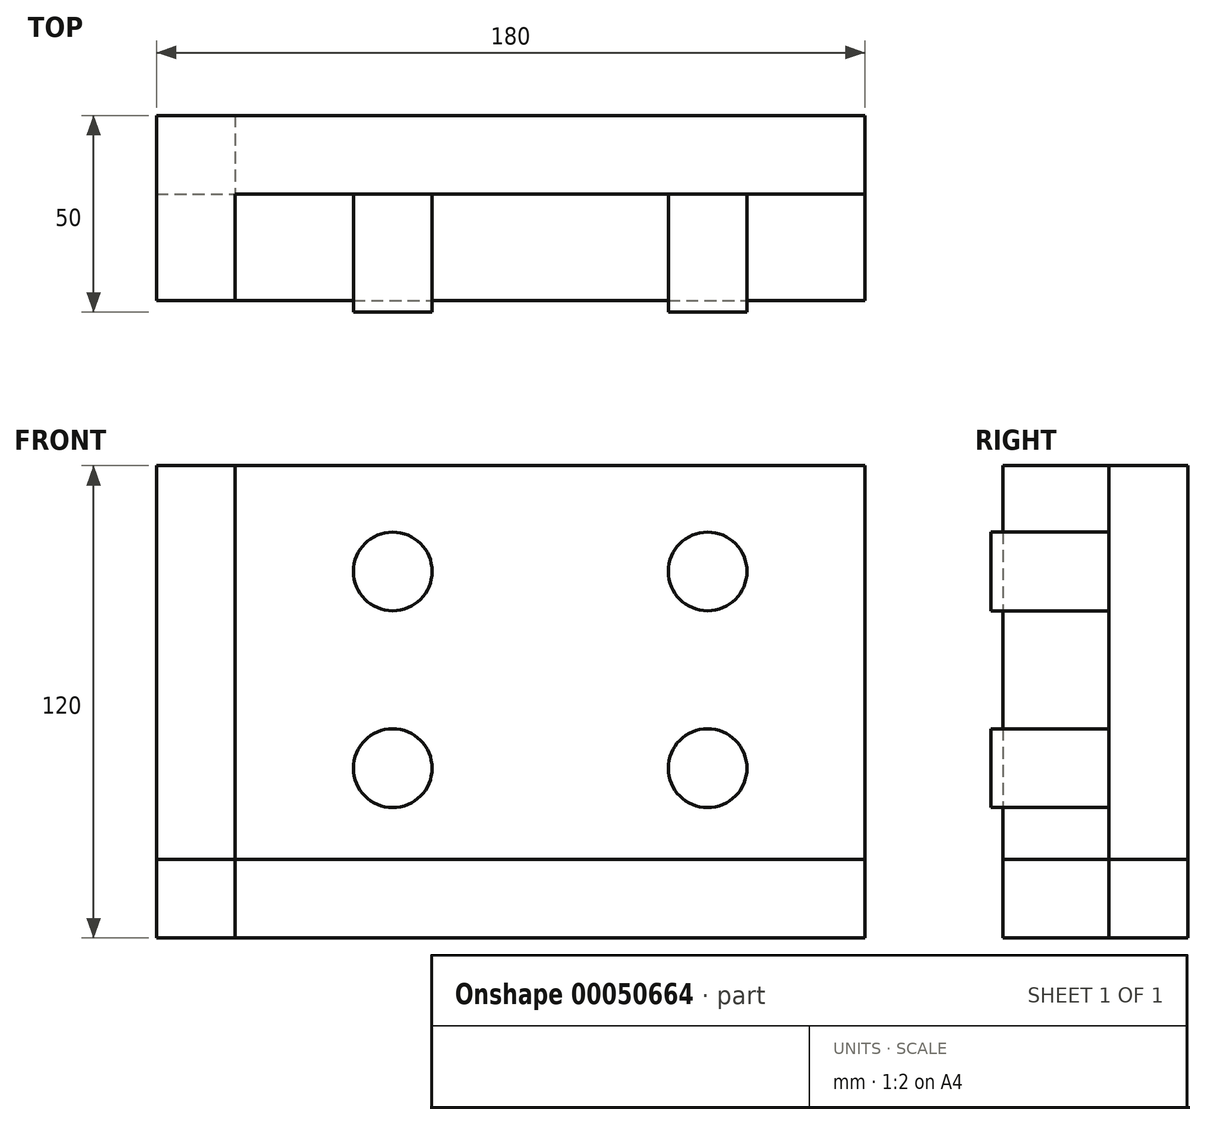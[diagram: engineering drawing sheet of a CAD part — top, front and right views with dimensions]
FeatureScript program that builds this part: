
annotation { "Feature Type Name" : "Feature", "Feature Type Description" : "" }
export const myFeature = defineFeature(function(context is Context, id is Id, definition is map)
    precondition{}
    {
        {
            var Q0;
            Q0=qCreatedBy(makeId("Front.planeOp"),FACE);
            var sketch = newSketch(context, id + "F0", { "sketchPlane" : qUnion([Q0])});
            skLineSegment(sketch, "E0.bottom", {"start": v(-80, 50) * mm, "end": v(80, 50) * mm});
            skLineSegment(sketch, "E0.top", {"start": v(-80, -50) * mm, "end": v(80, -50) * mm});
            skLineSegment(sketch, "E0.left", {"start": v(-80, 50) * mm, "end": v(-80, -50) * mm});
            skLineSegment(sketch, "E0.right", {"start": v(80, 50) * mm, "end": v(80, -50) * mm});
            skSolve(sketch);
        }
        {
            var Q0;
            Q0=makeQuery(id+"F0.imprint","IMPRINT",FACE,{"disambiguationData":[TD([[makeQuery(id+"F0.imprint","IMPRINT",EDGE,{"derivedFrom":sQuery(id+"F0.wireOp",EDGE,"E0.bottom")}),-1.0]])]});
            extrude(context, id + "F1", {"entities" : qUnion([Q0]), "oppositeDirection" : true, "depth" : 20 * mm});
        }
        {
            var Q0;
            Q0=qCreatedBy(makeId("Right.planeOp"),FACE);
            cPlane(context, id + "F2", {"entities" : qUnion([Q0]), "cplaneType" : CPlaneType.OFFSET, "offset" : 80 * mm, "oppositeDirection" : true, "width" : 150 * mm, "height" : 150 * mm});
        }
        {
            var Q0;
            Q0=qCreatedBy(id+"F2.planeOp",FACE);
            var sketch = newSketch(context, id + "F3", { "sketchPlane" : qUnion([Q0])});
            skLineSegment(sketch, "E1.bottom", {"start": v(-27, 50) * mm, "end": v(0, 50) * mm});
            skLineSegment(sketch, "E1.top", {"start": v(-27, -50) * mm, "end": v(0, -50) * mm});
            skLineSegment(sketch, "E1.left", {"start": v(-27, 50) * mm, "end": v(-27, -50) * mm});
            skLineSegment(sketch, "E1.right", {"start": v(0, 50) * mm, "end": v(0, -50) * mm});
            skSolve(sketch);
        }
        {
            var Q0;
            Q0=makeQuery(id+"F3.imprint","IMPRINT",FACE,{"disambiguationData":[TD([[makeQuery(id+"F3.imprint","IMPRINT",EDGE,{"derivedFrom":sQuery(id+"F3.wireOp",EDGE,"E1.bottom")}),-1.0]])]});
            extrude(context, id + "F4", {"entities" : qUnion([Q0]), "operationType" : NewBodyOperationType.ADD, "oppositeDirection" : true, "depth" : 20 * mm});
        }
        {
            var Q0;
            Q0=makeQuery(id+"F4.opExtrude","SWEPT_FACE",FACE,{"disambiguationData":[OSD([sQuery(id+"F3.wireOp",EDGE,"E1.left")])]});
            var Q1;
            Q1=makeQuery(id+"F4.opExtrude","SWEPT_FACE",FACE,{"disambiguationData":[OSD([sQuery(id+"F3.wireOp",EDGE,"E1.right")])]});
            extrude(context, id + "F5", {"entities" : qUnion([Q0, Q1]), "operationType" : NewBodyOperationType.ADD, "oppositeDirection" : true, "depth" : 20 * mm});
        }
        {
            var Q0;
            Q0=makeQuery(id+"F1.opExtrude","CAP_FACE",FACE,{"disambiguationData":[OSD([sQuery(id+"F0.wireOp",EDGE,"E0.bottom"),sQuery(id+"F0.wireOp",EDGE,"E0.top"),sQuery(id+"F0.wireOp",EDGE,"E0.left"),sQuery(id+"F0.wireOp",EDGE,"E0.right")])],"isStart":true});
            var sketch = newSketch(context, id + "F6", { "sketchPlane" : qUnion([Q0])});
            skCircle(sketch, "E2", {"center": v(-40, -26.85) * mm, "radius": 10 * mm});
            skCircle(sketch, "E3.0.1.0", {"center": v(-40, 23.15) * mm, "radius": 10 * mm});
            skCircle(sketch, "E3.1.0.0", {"center": v(40, -26.85) * mm, "radius": 10 * mm});
            skCircle(sketch, "E3.1.1.0", {"center": v(40, 23.15) * mm, "radius": 10 * mm});
            skLineSegment(sketch, "E3.direction1", {"start": v(-40, -26.85) * mm, "end": v(40, -26.85) * mm, "construction": true});
            skLineSegment(sketch, "E3.direction2", {"start": v(-40, -26.85) * mm, "end": v(-40, 23.15) * mm, "construction": true});
            skSolve(sketch);
        }
        {
            var Q0;
            Q0 = qSketchRegion(id + "F6", true);
            extrude(context, id + "F7", {"entities" : qUnion([Q0]), "operationType" : NewBodyOperationType.ADD, "depth" : 30 * mm});
        }
        {
            var Q0;
            Q0=qCreatedBy(makeId("Top.planeOp"),FACE);
            cPlane(context, id + "F8", {"entities" : qUnion([Q0]), "cplaneType" : CPlaneType.OFFSET, "offset" : 50 * mm, "oppositeDirection" : true, "width" : 150 * mm, "height" : 150 * mm});
        }
        {
            var Q0;
            Q0=qCreatedBy(id+"F8.planeOp",FACE);
            var sketch = newSketch(context, id + "F9", { "sketchPlane" : qUnion([Q0])});
            skLineSegment(sketch, "E4.bottom", {"start": v(-80, 0) * mm, "end": v(80, 0) * mm});
            skLineSegment(sketch, "E4.top", {"start": v(-80, -27) * mm, "end": v(80, -27) * mm});
            skLineSegment(sketch, "E4.left", {"start": v(-80, 0) * mm, "end": v(-80, -27) * mm});
            skLineSegment(sketch, "E4.right", {"start": v(80, 0) * mm, "end": v(80, -27) * mm});
            skSolve(sketch);
        }
        {
            var Q0;
            Q0=makeQuery(id+"F9.imprint","IMPRINT",FACE,{"disambiguationData":[TD([[makeQuery(id+"F9.imprint","IMPRINT",EDGE,{"derivedFrom":sQuery(id+"F9.wireOp",EDGE,"E4.bottom")}),-1.0]])]});
            extrude(context, id + "F10", {"entities" : qUnion([Q0]), "oppositeDirection" : true, "depth" : 20 * mm});
        }
        {
            var Q0;
            Q0=makeQuery(id+"F10.opExtrude","SWEPT_FACE",FACE,{"disambiguationData":[OSD([sQuery(id+"F9.wireOp",EDGE,"E4.bottom")])]});
            var Q1;
            Q1=makeQuery(id+"F1.opExtrude","CAP_FACE",FACE,{"disambiguationData":[OSD([sQuery(id+"F0.wireOp",EDGE,"E0.bottom"),sQuery(id+"F0.wireOp",EDGE,"E0.top"),sQuery(id+"F0.wireOp",EDGE,"E0.left"),sQuery(id+"F0.wireOp",EDGE,"E0.right")])],"isStart":false});
            extrude(context, id + "F11", {"entities" : qUnion([Q0]), "endBound" : BoundingType.UP_TO_SURFACE, "endBoundEntityFace" : qUnion([Q1]), "depth" : 25 * mm});
        }
        {
            var Q0;
            Q0=makeQuery(id+"F10.opExtrude","SWEPT_FACE",FACE,{"disambiguationData":[OSD([sQuery(id+"F9.wireOp",EDGE,"E4.left")])]});
            var Q1;
            {var subQ0=sQuery(id+"F3.wireOp",EDGE,"E1.right");Q1=makeQuery(id+"F5.boolean.opBoolean","MERGE",FACE,{"derivedFrom":[makeQuery(id+"F4.opExtrude","CAP_FACE",FACE,{"disambiguationData":[OSD([sQuery(id+"F3.wireOp",EDGE,"E1.bottom"),sQuery(id+"F3.wireOp",EDGE,"E1.top"),sQuery(id+"F3.wireOp",EDGE,"E1.left"),subQ0])],"isStart":false}),makeQuery(id+"F5.opExtrude","SWEPT_FACE",FACE,{"disambiguationData":[OSD([subQ0]),TDD([makeQuery(id+"F4.opExtrude","CAP_EDGE",EDGE,{"disambiguationData":[OSD([subQ0])],"isStart":false})])]})]});}
            extrude(context, id + "F12", {"entities" : qUnion([Q0]), "endBound" : BoundingType.UP_TO_SURFACE, "endBoundEntityFace" : qUnion([Q1]), "depth" : 25 * mm});
        }
        {
            var Q0;
            Q0=makeQuery(id+"F11.opExtrude","SWEPT_FACE",FACE,{"disambiguationData":[OSD([sQuery(id+"F9.wireOp",EDGE,"E4.bottom"),sQuery(id+"F9.wireOp",EDGE,"E4.left")])]});
            var Q1;
            {var subQ0=sQuery(id+"F3.wireOp",EDGE,"E1.right");Q1=makeQuery(id+"F5.boolean.opBoolean","MERGE",FACE,{"derivedFrom":[makeQuery(id+"F4.opExtrude","CAP_FACE",FACE,{"disambiguationData":[OSD([sQuery(id+"F3.wireOp",EDGE,"E1.bottom"),sQuery(id+"F3.wireOp",EDGE,"E1.top"),sQuery(id+"F3.wireOp",EDGE,"E1.left"),subQ0])],"isStart":false}),makeQuery(id+"F5.opExtrude","SWEPT_FACE",FACE,{"disambiguationData":[OSD([subQ0]),TDD([makeQuery(id+"F4.opExtrude","CAP_EDGE",EDGE,{"disambiguationData":[OSD([subQ0])],"isStart":false})])]})]});}
            extrude(context, id + "F13", {"entities" : qUnion([Q0]), "endBound" : BoundingType.UP_TO_SURFACE, "endBoundEntityFace" : qUnion([Q1]), "depth" : 25 * mm});
        }
    });
